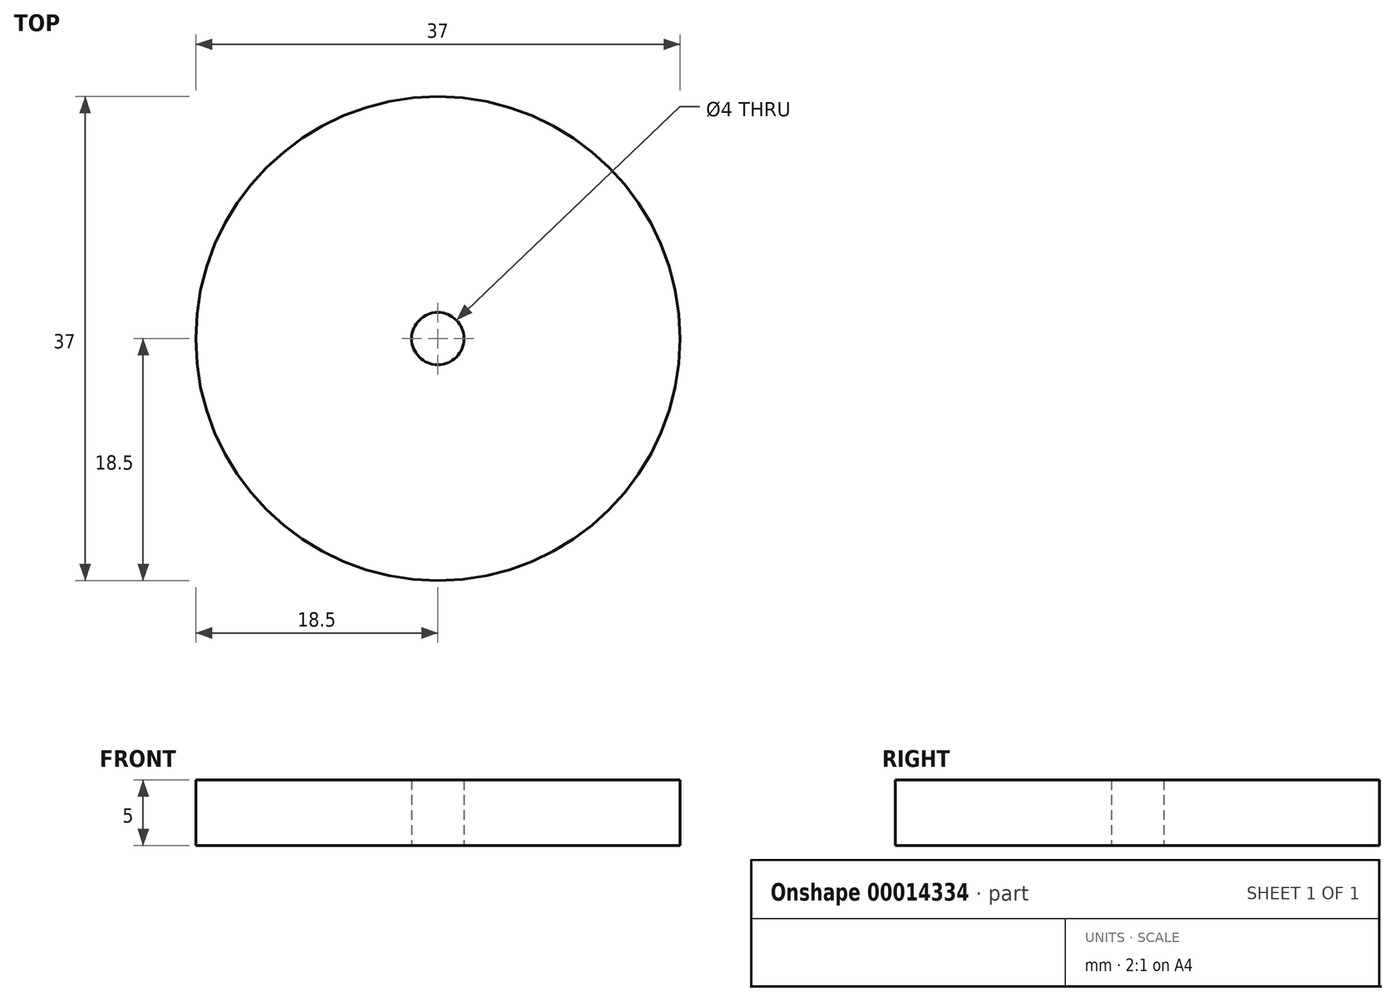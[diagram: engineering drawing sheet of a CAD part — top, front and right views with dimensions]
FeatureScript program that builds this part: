
annotation { "Feature Type Name" : "Feature", "Feature Type Description" : "" }
export const myFeature = defineFeature(function(context is Context, id is Id, definition is map)
    precondition{}
    {
        {
            var Q0;
            Q0=qCreatedBy(makeId("Top.planeOp"),FACE);
            var sketch = newSketch(context, id + "F0", { "sketchPlane" : qUnion([Q0])});
            skCircle(sketch, "E0", {"center": v(0, 0) * mm, "radius": 18.5 * mm});
            skCircle(sketch, "E1", {"center": v(0, 0) * mm, "radius": 2 * mm});
            skSolve(sketch);
        }
        {
            var Q0;
            Q0=makeQuery(id+"F0.imprint","IMPRINT",FACE,{"disambiguationData":[TD([[makeQuery(id+"F0.imprint","IMPRINT",EDGE,{"derivedFrom":sQuery(id+"F0.wireOp",EDGE,"E0")}),1.0]])]});
            extrude(context, id + "F1", {"entities" : qUnion([Q0]), "depth" : 5 * mm});
        }
    });
